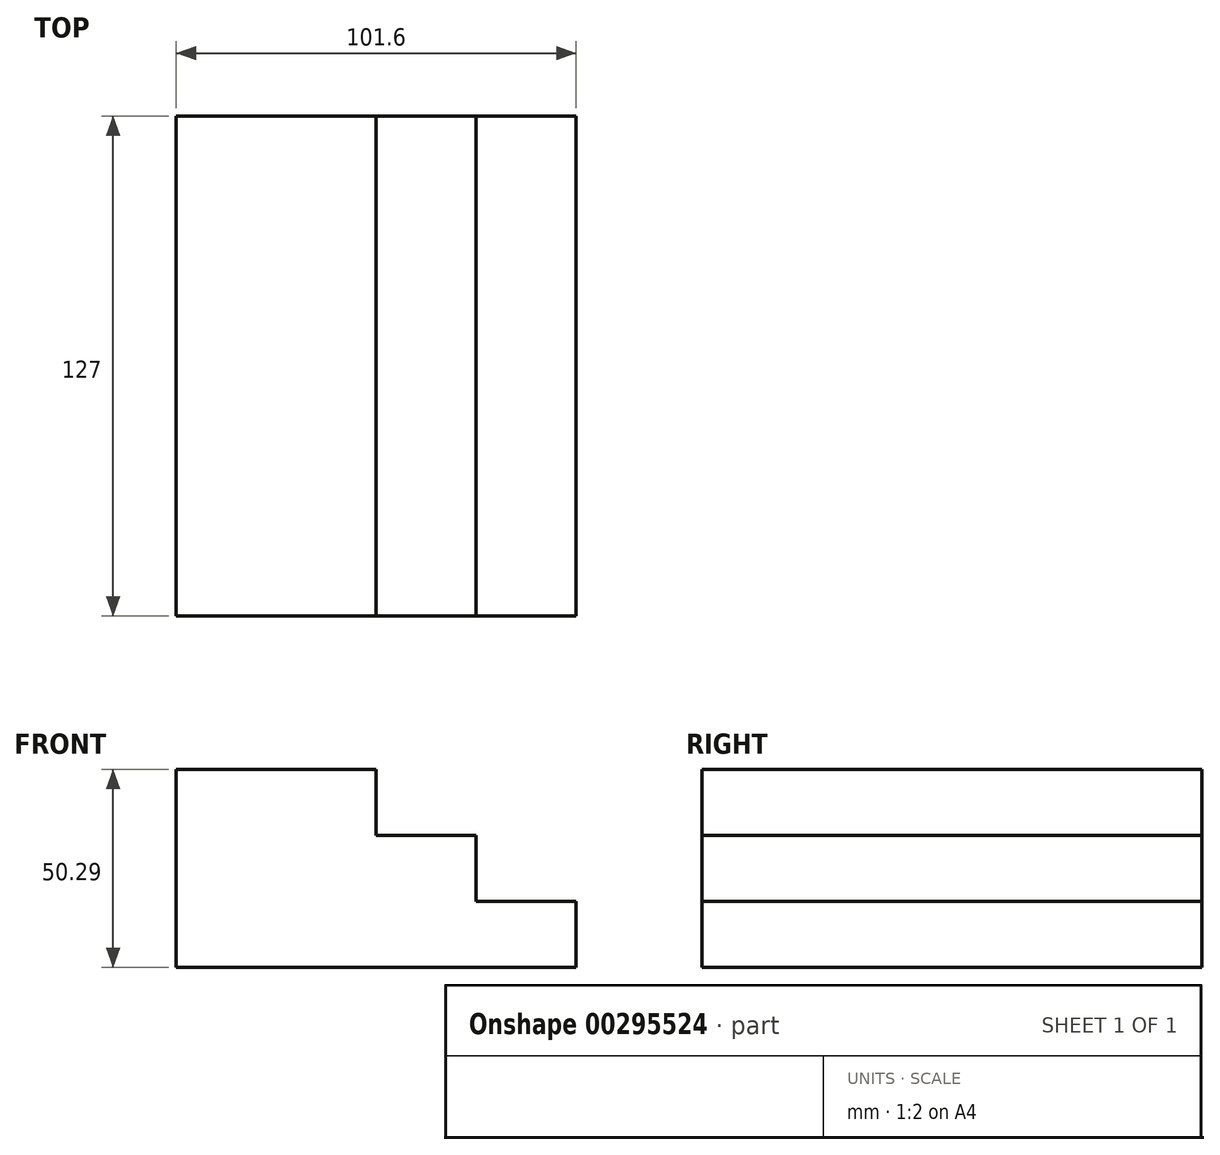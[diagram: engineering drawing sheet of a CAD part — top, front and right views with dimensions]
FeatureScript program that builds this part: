
annotation { "Feature Type Name" : "Feature", "Feature Type Description" : "" }
export const myFeature = defineFeature(function(context is Context, id is Id, definition is map)
    precondition{}
    {
        {
            var Q0;
            Q0=qCreatedBy(makeId("Front.planeOp"),FACE);
            var sketch = newSketch(context, id + "F0", { "sketchPlane" : qUnion([Q0])});
            skLineSegment(sketch, "E0.bottom", {"start": v(0, 0) * mm, "end": v(50.8, 0) * mm});
            skLineSegment(sketch, "E0.top", {"start": v(0, -16.76) * mm, "end": v(50.8, -16.76) * mm});
            skLineSegment(sketch, "E0.left", {"start": v(0, 0) * mm, "end": v(0, -16.76) * mm});
            skLineSegment(sketch, "E0.right", {"start": v(50.8, 0) * mm, "end": v(50.8, -16.76) * mm});
            skLineSegment(sketch, "E1.bottom", {"start": v(0, -16.76) * mm, "end": v(76.2, -16.76) * mm});
            skLineSegment(sketch, "E1.top", {"start": v(0, -33.53) * mm, "end": v(76.2, -33.53) * mm});
            skLineSegment(sketch, "E1.left", {"start": v(0, -16.76) * mm, "end": v(0, -33.53) * mm});
            skLineSegment(sketch, "E1.right", {"start": v(76.2, -16.76) * mm, "end": v(76.2, -33.53) * mm});
            skLineSegment(sketch, "E2.bottom", {"start": v(0, -33.53) * mm, "end": v(101.6, -33.53) * mm});
            skLineSegment(sketch, "E2.top", {"start": v(0, -50.3) * mm, "end": v(101.6, -50.3) * mm});
            skLineSegment(sketch, "E2.left", {"start": v(0, -33.53) * mm, "end": v(0, -50.3) * mm});
            skLineSegment(sketch, "E2.right", {"start": v(101.6, -33.53) * mm, "end": v(101.6, -50.3) * mm});
            skSolve(sketch);
        }
        {
            var Q0;
            Q0 = qSketchRegion(id + "F0", true);
            extrude(context, id + "F1", {"entities" : qUnion([Q0]), "depth" : 127 * mm});
        }
    });
